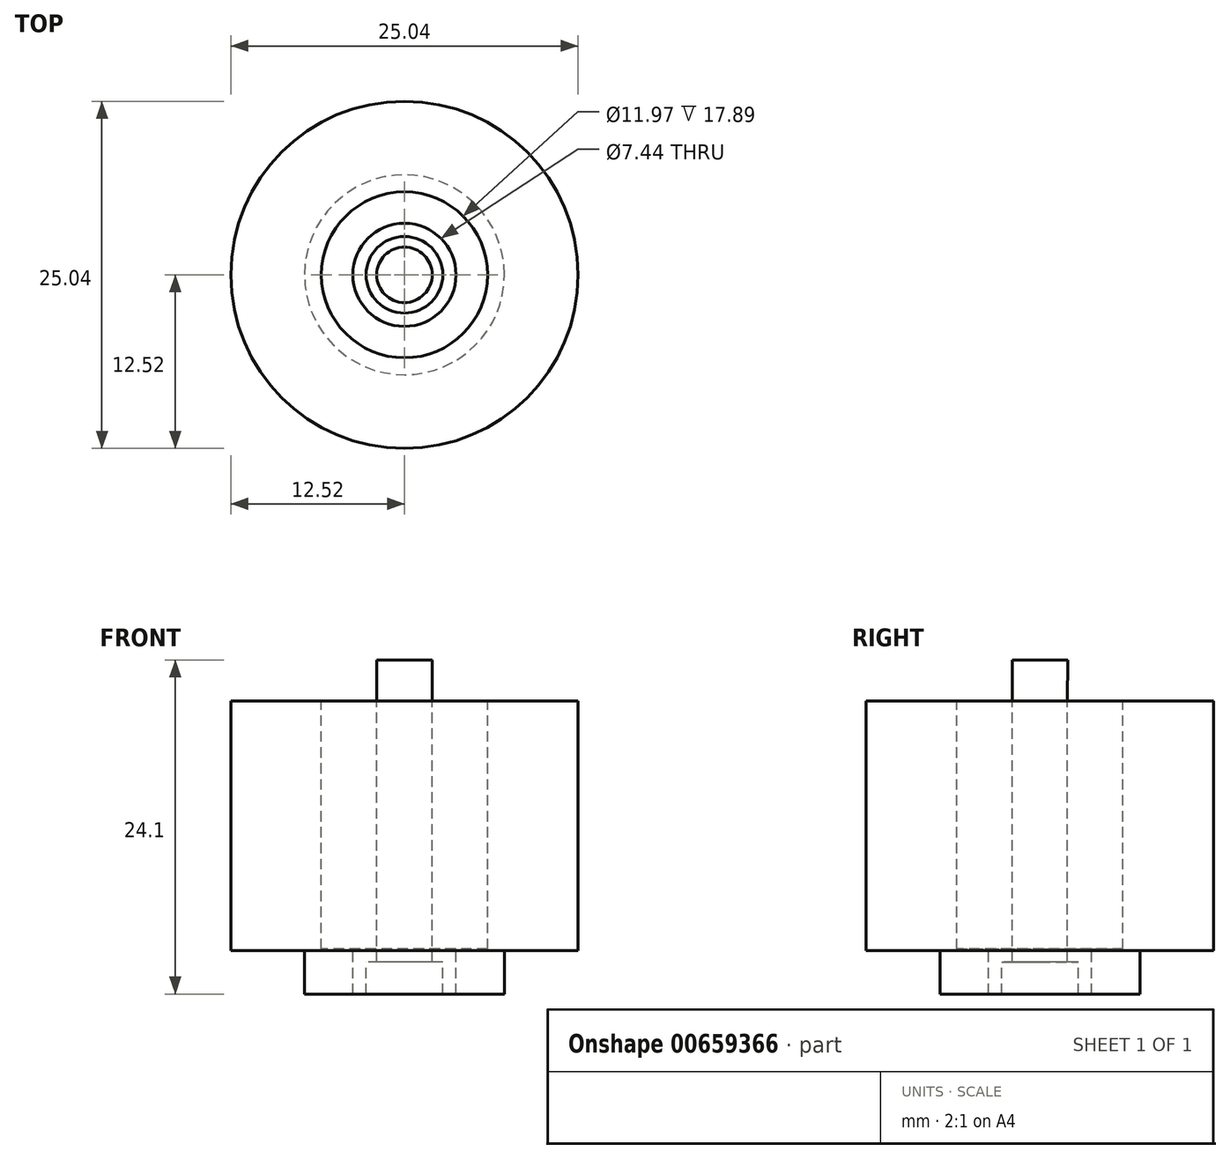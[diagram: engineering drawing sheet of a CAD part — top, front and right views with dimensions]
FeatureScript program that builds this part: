
annotation { "Feature Type Name" : "Feature", "Feature Type Description" : "" }
export const myFeature = defineFeature(function(context is Context, id is Id, definition is map)
    precondition{}
    {
        {
            var Q0;
            Q0=qCreatedBy(makeId("Front.planeOp"),FACE);
            var sketch = newSketch(context, id + "F0", { "sketchPlane" : qUnion([Q0])});
            skLineSegment(sketch, "E0", {"start": v(0, 12.1) * mm, "end": v(0, -12.01) * mm});
            skLineSegment(sketch, "E1", {"start": v(0, -12.01) * mm, "end": v(7.2, -12.01) * mm});
            skLineSegment(sketch, "E2", {"start": v(7.2, -12.01) * mm, "end": v(7.2, -8.89) * mm});
            skLineSegment(sketch, "E3", {"start": v(12.52, -8.89) * mm, "end": v(7.2, -8.89) * mm});
            skLineSegment(sketch, "E4", {"start": v(12.52, -8.89) * mm, "end": v(12.52, 13.65) * mm});
            skLineSegment(sketch, "E5", {"start": v(1.99, 9.13) * mm, "end": v(1.99, -9.71) * mm});
            skLineSegment(sketch, "E6", {"start": v(1.99, -9.71) * mm, "end": v(2.76, -9.71) * mm});
            skLineSegment(sketch, "E7", {"start": v(2.76, -9.71) * mm, "end": v(2.76, -12.01) * mm});
            skLineSegment(sketch, "E8", {"start": v(1.99, 9.13) * mm, "end": v(12.52, 9.13) * mm});
            skLineSegment(sketch, "E9", {"start": v(12.52, 9.15) * mm, "end": v(12.52, 9.13) * mm});
            skLineSegment(sketch, "E10", {"start": v(2.76, -12.01) * mm, "end": v(0, -12.01) * mm});
            skLineSegment(sketch, "E11", {"start": v(1.99, 9.13) * mm, "end": v(5.99, 9.13) * mm});
            skLineSegment(sketch, "E12", {"start": v(5.99, 9.13) * mm, "end": v(5.99, -8.76) * mm});
            skLineSegment(sketch, "E13", {"start": v(3.72, -8.76) * mm, "end": v(5.99, -8.76) * mm});
            skLineSegment(sketch, "E14", {"start": v(3.72, -8.76) * mm, "end": v(3.72, -12.01) * mm});
            skLineSegment(sketch, "E15", {"start": v(0, 12.1) * mm, "end": v(2, 12.1) * mm});
            skLineSegment(sketch, "E16", {"start": v(2, 12.1) * mm, "end": v(1.99, 9.13) * mm});
            skSolve(sketch);
        }
        {
            var Q0;
            {var subQ2=sQuery(id+"F0.wireOp",EDGE,"E2");Q0=makeQuery(id+"F0.imprint","IMPRINT",FACE,{"disambiguationData":[TD([[makeQuery(id+"F0.imprint","IMPRINT",EDGE,{"derivedFrom":subQ2}),1.0]])]});}
            var Q1;
            Q1=sQuery(id+"F0.wireOp",EDGE,"E0");
            revolve(context, id + "F1", {"entities" : qUnion([Q0]), "axis" : qUnion([Q1]), "revolveType" : RevolveType.FULL});
        }
        {
            var Q0;
            Q0=makeQuery(id+"F0.imprint","IMPRINT",FACE,{"disambiguationData":[TD([[makeQuery(id+"F0.imprint","IMPRINT",EDGE,{"derivedFrom":sQuery(id+"F0.wireOp",EDGE,"E5")}),-1.0]])]});
            var Q1;
            Q1=sQuery(id+"F0.wireOp",EDGE,"E0");
            revolve(context, id + "F2", {"entities" : qUnion([Q0]), "axis" : qUnion([Q1]), "revolveType" : RevolveType.FULL});
        }
    });
